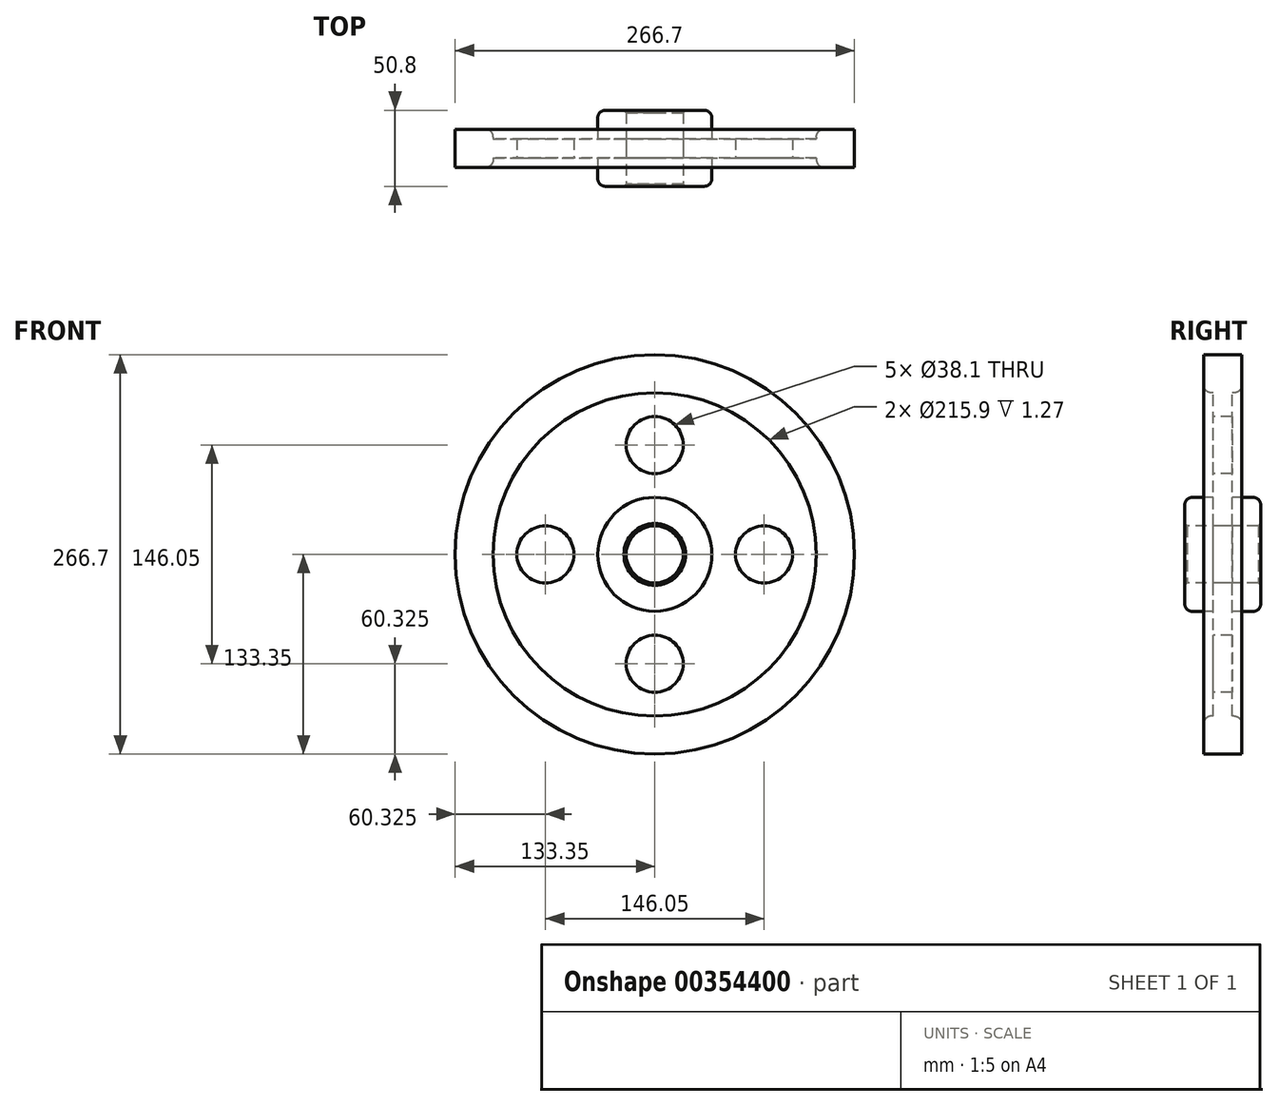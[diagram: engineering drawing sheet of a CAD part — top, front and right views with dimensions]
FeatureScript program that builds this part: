
annotation { "Feature Type Name" : "Feature", "Feature Type Description" : "" }
export const myFeature = defineFeature(function(context is Context, id is Id, definition is map)
    precondition{}
    {
        {
            var Q0;
            Q0=qCreatedBy(makeId("Right.planeOp"),FACE);
            var sketch = newSketch(context, id + "F0", { "sketchPlane" : qUnion([Q0])});
            skLineSegment(sketch, "E0", {"start": v(0, 0) * mm, "end": v(75.27, 0) * mm, "construction": true});
            skLineSegment(sketch, "E1.0", {"start": v(0, 19.05) * mm, "end": v(25.4, 19.05) * mm});
            skLineSegment(sketch, "E2.0", {"start": v(6.35, 38.1) * mm, "end": v(25.4, 38.1) * mm});
            skLineSegment(sketch, "E3.0", {"start": v(6.35, 107.95) * mm, "end": v(12.7, 107.95) * mm});
            skLineSegment(sketch, "E4.0", {"start": v(0, 133.35) * mm, "end": v(12.7, 133.35) * mm});
            skLineSegment(sketch, "E5", {"start": v(0, 133.35) * mm, "end": v(0, 0) * mm, "construction": true});
            skLineSegment(sketch, "E6.0", {"start": v(25.4, 38.1) * mm, "end": v(25.4, 19.05) * mm});
            skLineSegment(sketch, "E7.0", {"start": v(12.7, 133.35) * mm, "end": v(12.7, 107.95) * mm});
            skLineSegment(sketch, "E8.0", {"start": v(6.35, 107.95) * mm, "end": v(6.35, 38.1) * mm});
            skLineSegment(sketch, "E9.MirrorCS", {"start": v(0, 133.35) * mm, "end": v(-12.7, 133.35) * mm});
            skLineSegment(sketch, "E10.MirrorCS", {"start": v(-12.7, 133.35) * mm, "end": v(-12.7, 107.95) * mm});
            skLineSegment(sketch, "E11.MirrorCS", {"start": v(-6.35, 107.95) * mm, "end": v(-12.7, 107.95) * mm});
            skLineSegment(sketch, "E12.MirrorCS", {"start": v(-6.35, 107.95) * mm, "end": v(-6.35, 38.1) * mm});
            skLineSegment(sketch, "E13.MirrorCS", {"start": v(-6.35, 38.1) * mm, "end": v(-25.4, 38.1) * mm});
            skLineSegment(sketch, "E14.MirrorCS", {"start": v(-25.4, 38.1) * mm, "end": v(-25.4, 19.05) * mm});
            skLineSegment(sketch, "E15.MirrorCS", {"start": v(0, 19.05) * mm, "end": v(-25.4, 19.05) * mm});
            skSolve(sketch);
        }
        {
            var Q0;
            Q0=makeQuery(id+"F0.imprint","IMPRINT",FACE,{"disambiguationData":[TD([[makeQuery(id+"F0.imprint","IMPRINT",EDGE,{"derivedFrom":sQuery(id+"F0.wireOp",EDGE,"E1.0")}),1.0]])]});
            var Q1;
            Q1=sQuery(id+"F0.wireOp",EDGE,"E0");
            revolve(context, id + "F1", {"entities" : qUnion([Q0]), "axis" : qUnion([Q1]), "revolveType" : RevolveType.FULL});
        }
        {
            var Q0;
            Q0=makeQuery(id+"F1.opRevolve","SWEPT_FACE",FACE,{"disambiguationData":[OSD([sQuery(id+"F0.wireOp",EDGE,"E12.MirrorCS")])]});
            var sketch = newSketch(context, id + "F2", { "sketchPlane" : qUnion([Q0])});
            skLineSegment(sketch, "E16", {"start": v(0, 0) * mm, "end": v(0, 73.03) * mm});
            skCircle(sketch, "E17", {"center": v(0, 73.03) * mm, "radius": 19.05 * mm});
            skCircle(sketch, "E18.1.0", {"center": v(-73.03, 0) * mm, "radius": 19.05 * mm});
            skCircle(sketch, "E18.2.0", {"center": v(0, -73.03) * mm, "radius": 19.05 * mm});
            skCircle(sketch, "E18.3.0", {"center": v(73.03, 0) * mm, "radius": 19.05 * mm});
            skPoint(sketch, "E18.center", {"position": v(0, 0) * mm});
            skSolve(sketch);
        }
        {
            var Q0;
            Q0=makeQuery(id+"F2.imprint","IMPRINT",FACE,{"disambiguationData":[TD([[makeQuery(id+"F2.imprint","IMPRINT",EDGE,{"derivedFrom":sQuery(id+"F2.wireOp",EDGE,"E17")}),1.0]])]});
            var Q1;
            Q1=makeQuery(id+"F2.imprint","IMPRINT",FACE,{"disambiguationData":[TD([[makeQuery(id+"F2.imprint","IMPRINT",EDGE,{"derivedFrom":sQuery(id+"F2.wireOp",EDGE,"E18.3.0")}),1.0]])]});
            var Q2;
            Q2=makeQuery(id+"F2.imprint","IMPRINT",FACE,{"disambiguationData":[TD([[makeQuery(id+"F2.imprint","IMPRINT",EDGE,{"derivedFrom":sQuery(id+"F2.wireOp",EDGE,"E18.2.0")}),1.0]])]});
            var Q3;
            Q3=makeQuery(id+"F2.imprint","IMPRINT",FACE,{"disambiguationData":[TD([[makeQuery(id+"F2.imprint","IMPRINT",EDGE,{"derivedFrom":sQuery(id+"F2.wireOp",EDGE,"E18.1.0")}),1.0]])]});
            extrude(context, id + "F3", {"entities" : qUnion([Q0, Q1, Q2, Q3]), "operationType" : NewBodyOperationType.REMOVE, "oppositeDirection" : true, "depth" : 25.4 * mm});
        }
        {
            var Q0;
            Q0=makeQuery(id+"F1.opRevolve","SWEPT_EDGE",EDGE,{"disambiguationData":[OSD([sQuery(id+"F0.wireOp",EDGE,"E13.MirrorCS"),sQuery(id+"F0.wireOp",EDGE,"E14.MirrorCS")])]});
            var Q1;
            Q1=makeQuery(id+"F1.opRevolve","SWEPT_EDGE",EDGE,{"disambiguationData":[OSD([sQuery(id+"F0.wireOp",EDGE,"E10.MirrorCS"),sQuery(id+"F0.wireOp",EDGE,"E11.MirrorCS")])]});
            var Q2;
            Q2=makeQuery(id+"F1.opRevolve","SWEPT_EDGE",EDGE,{"disambiguationData":[OSD([sQuery(id+"F0.wireOp",EDGE,"E2.0"),sQuery(id+"F0.wireOp",EDGE,"E6.0")])]});
            var Q3;
            Q3=makeQuery(id+"F1.opRevolve","SWEPT_EDGE",EDGE,{"disambiguationData":[OSD([sQuery(id+"F0.wireOp",EDGE,"E3.0"),sQuery(id+"F0.wireOp",EDGE,"E7.0")])]});
            fillet(context, id + "F4", {"entities" : qUnion([Q0, Q1, Q2, Q3]), "radius" : 5.08 * mm, "tangentPropagation" : true, "allowEdgeOverflow" : false});
        }
        {
            var Q0;
            Q0=makeQuery(id+"F1.opRevolve","SWEPT_EDGE",EDGE,{"disambiguationData":[OSD([sQuery(id+"F0.wireOp",EDGE,"E14.MirrorCS"),sQuery(id+"F0.wireOp",EDGE,"E15.MirrorCS")])]});
            var Q1;
            Q1=makeQuery(id+"F1.opRevolve","SWEPT_EDGE",EDGE,{"disambiguationData":[OSD([sQuery(id+"F0.wireOp",EDGE,"E1.0"),sQuery(id+"F0.wireOp",EDGE,"E6.0")])]});
            chamfer(context, id + "F5", {"entities" : qUnion([Q0, Q1]), "width" : 1.59 * mm, "tangentPropagation" : true});
        }
    });
